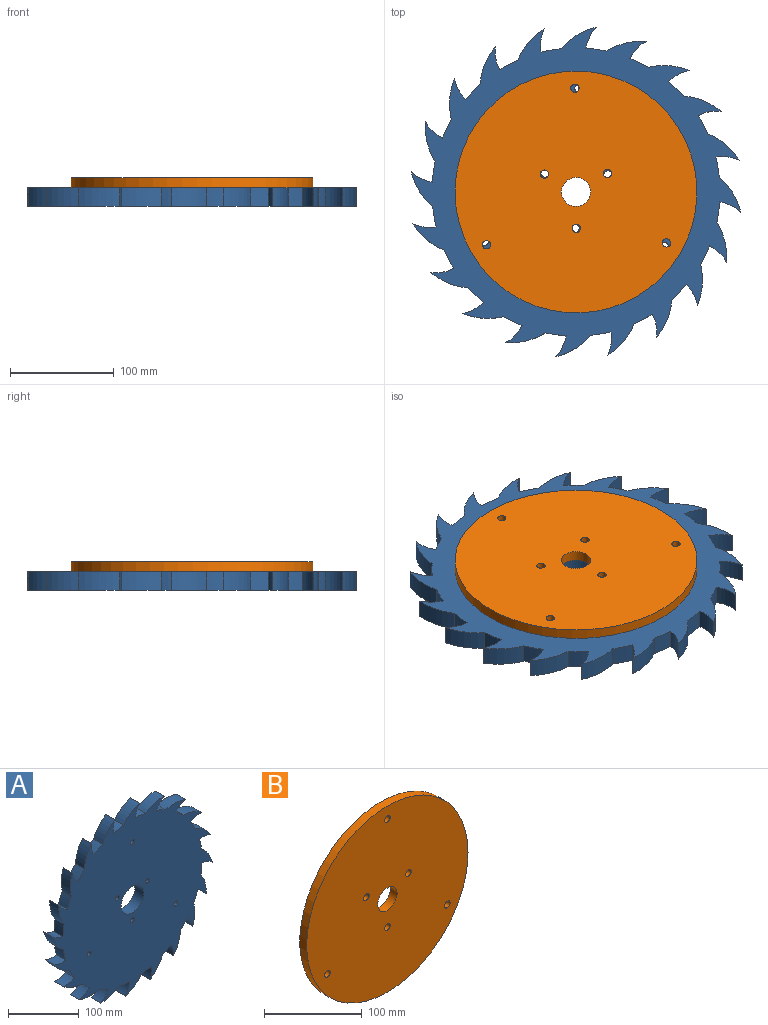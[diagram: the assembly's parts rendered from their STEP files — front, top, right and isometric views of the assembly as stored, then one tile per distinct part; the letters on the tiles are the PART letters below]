
ASSEMBLY  parts=2 mates=1
PART A: 69 faces, bbox 318.6x18x318.6 mm
  f0: cylinder r=138.84mm len=19.46mm, axis (0,1,0), area 357.8mm2, adj f1,f66,f67,f68
  f1: cylinder r=38.2mm len=22.42mm, axis (0,1,0), area 412mm2, adj f0,f2,f67,f68
  f2: cylinder r=63.8mm len=30.75mm, axis (0,1,0), area 720.6mm2, adj f1,f3,f67,f68
  f3: cylinder r=138.84mm len=18mm, axis (0,1,0), area 357.8mm2, adj f2,f4,f67,f68
  f4: cylinder r=38.2mm len=22.06mm, axis (0,1,0), area 412mm2, adj f3,f5,f67,f68
  f5: cylinder r=63.8mm len=36.85mm, axis (0,1,0), area 720.6mm2, adj f4,f6,f67,f68
  f6: cylinder r=138.84mm len=18mm, axis (0,1,0), area 357.8mm2, adj f5,f7,f67,f68
  f7: cylinder r=38.2mm len=19.55mm, axis (0,1,0), area 412mm2, adj f6,f8,f67,f68
  f8: cylinder r=63.8mm len=39.34mm, axis (0,1,0), area 720.6mm2, adj f7,f9,f67,f68
  f9: cylinder r=138.84mm len=18.08mm, axis (0,1,0), area 357.8mm2, adj f8,f10,f67,f68
  f10: cylinder r=38.2mm len=18mm, axis (0,1,0), area 412mm2, adj f9,f11,f67,f68
  f11: cylinder r=63.8mm len=37.98mm, axis (0,1,0), area 720.6mm2, adj f10,f12,f67,f68
  f12: cylinder r=138.84mm len=19.73mm, axis (0,1,0), area 357.8mm2, adj f11,f13,f67,f68
  f13: cylinder r=38.2mm len=20.58mm, axis (0,1,0), area 412mm2, adj f12,f14,f67,f68
  f14: cylinder r=63.8mm len=32.9mm, axis (0,1,0), area 720.6mm2, adj f13,f15,f67,f68
  f15: cylinder r=138.84mm len=19.46mm, axis (0,1,0), area 357.8mm2, adj f14,f16,f67,f68
  f16: cylinder r=38.2mm len=22.42mm, axis (0,1,0), area 412mm2, adj f15,f17,f67,f68
  f17: cylinder r=63.8mm len=30.75mm, axis (0,1,0), area 720.6mm2, adj f16,f18,f67,f68
  f18: cylinder r=138.84mm len=18mm, axis (0,1,0), area 357.8mm2, adj f17,f19,f67,f68
  f19: cylinder r=38.2mm len=22.06mm, axis (0,1,0), area 412mm2, adj f18,f20,f67,f68
  f20: cylinder r=63.8mm len=36.85mm, axis (0,1,0), area 720.6mm2, adj f19,f21,f67,f68
  f21: cylinder r=138.84mm len=18mm, axis (0,1,0), area 357.8mm2, adj f20,f22,f67,f68
  f22: cylinder r=38.2mm len=19.55mm, axis (0,1,0), area 412mm2, adj f21,f23,f67,f68
  f23: cylinder r=63.8mm len=39.34mm, axis (0,1,0), area 720.6mm2, adj f22,f24,f67,f68
  f24: cylinder r=138.84mm len=18.08mm, axis (0,1,0), area 357.8mm2, adj f23,f25,f67,f68
  f25: cylinder r=38.2mm len=18mm, axis (0,1,0), area 412mm2, adj f24,f26,f67,f68
  f26: cylinder r=63.8mm len=37.98mm, axis (0,1,0), area 720.6mm2, adj f25,f27,f67,f68
  f27: cylinder r=138.84mm len=19.73mm, axis (0,1,0), area 357.8mm2, adj f26,f28,f67,f68
  f28: cylinder r=38.2mm len=20.58mm, axis (0,1,0), area 412mm2, adj f27,f29,f67,f68
  f29: cylinder r=63.8mm len=32.9mm, axis (0,1,0), area 720.6mm2, adj f28,f30,f67,f68
  f30: cylinder r=138.84mm len=19.46mm, axis (0,1,0), area 357.8mm2, adj f29,f31,f67,f68
  f31: cylinder r=38.2mm len=22.42mm, axis (0,1,0), area 412mm2, adj f30,f32,f67,f68
  f32: cylinder r=63.8mm len=30.75mm, axis (0,1,0), area 720.6mm2, adj f31,f33,f67,f68
  f33: cylinder r=138.84mm len=18mm, axis (0,1,0), area 357.8mm2, adj f32,f34,f67,f68
  f34: cylinder r=38.2mm len=22.06mm, axis (0,1,0), area 412mm2, adj f33,f35,f67,f68
  f35: cylinder r=63.8mm len=36.85mm, axis (0,1,0), area 720.6mm2, adj f34,f36,f67,f68
  f36: cylinder r=138.84mm len=18mm, axis (0,1,0), area 357.8mm2, adj f35,f37,f67,f68
  f37: cylinder r=38.2mm len=19.55mm, axis (0,1,0), area 412mm2, adj f36,f38,f67,f68
  f38: cylinder r=63.8mm len=39.34mm, axis (0,1,0), area 720.6mm2, adj f37,f39,f67,f68
  f39: cylinder r=138.84mm len=18.08mm, axis (0,1,0), area 357.8mm2, adj f38,f40,f67,f68
  f40: cylinder r=38.2mm len=18mm, axis (0,1,0), area 412mm2, adj f39,f41,f67,f68
  f41: cylinder r=63.8mm len=37.98mm, axis (0,1,0), area 720.6mm2, adj f40,f42,f67,f68
  f42: cylinder r=138.84mm len=19.73mm, axis (0,1,0), area 357.8mm2, adj f41,f43,f67,f68
  f43: cylinder r=38.2mm len=20.58mm, axis (0,1,0), area 412mm2, adj f42,f44,f67,f68
  f44: cylinder r=63.8mm len=32.9mm, axis (0,1,0), area 720.6mm2, adj f43,f45,f67,f68
  f45: cylinder r=138.84mm len=19.46mm, axis (0,1,0), area 357.8mm2, adj f44,f46,f67,f68
  f46: cylinder r=38.2mm len=22.42mm, axis (0,1,0), area 412mm2, adj f45,f47,f67,f68
  f47: cylinder r=63.8mm len=30.75mm, axis (0,1,0), area 720.6mm2, adj f46,f48,f67,f68
  f48: cylinder r=138.84mm len=18mm, axis (0,1,0), area 357.8mm2, adj f47,f49,f67,f68
  f49: cylinder r=38.2mm len=22.06mm, axis (0,1,0), area 412mm2, adj f48,f50,f67,f68
  f50: cylinder r=63.8mm len=36.85mm, axis (0,1,0), area 720.6mm2, adj f49,f51,f67,f68
  f51: cylinder r=138.84mm len=18mm, axis (0,1,0), area 357.8mm2, adj f50,f52,f67,f68
  f52: cylinder r=38.2mm len=19.55mm, axis (0,1,0), area 412mm2, adj f51,f53,f67,f68
  f53: cylinder r=63.8mm len=39.34mm, axis (0,1,0), area 720.6mm2, adj f52,f54,f67,f68
  f54: cylinder r=138.84mm len=18.08mm, axis (0,1,0), area 357.8mm2, adj f53,f55,f67,f68
  f55: cylinder r=38.2mm len=18mm, axis (0,1,0), area 412mm2, adj f54,f56,f67,f68
  f56: cylinder r=63.8mm len=37.98mm, axis (0,1,0), area 720.6mm2, adj f55,f57,f67,f68
  f57: cylinder r=138.84mm len=19.73mm, axis (0,1,0), area 357.8mm2, adj f56,f58,f67,f68
  f58: cylinder r=38.2mm len=20.58mm, axis (0,1,0), area 412mm2, adj f57,f66,f67,f68
  f59: cylinder r=4mm len=18mm, axis (0,1,0), area 452.4mm2, adj f67,f68
  f60: cylinder r=22.61mm len=45.21mm, axis (0,1,0), area 2556.7mm2, adj f67,f68
  f61: cylinder r=4mm len=18mm, axis (0,1,0), area 452.4mm2, adj f67,f68
  f62: cylinder r=4mm len=18mm, axis (0,1,0), area 452.4mm2, adj f67,f68
  f63: cylinder r=4mm len=18mm, axis (0,1,0), area 452.4mm2, adj f67,f68
  f64: cylinder r=4mm len=18mm, axis (0,1,0), area 452.4mm2, adj f67,f68
  f65: cylinder r=4mm len=18mm, axis (0,1,0), area 452.4mm2, adj f67,f68
  f66: cylinder r=63.8mm len=32.9mm, axis (0,1,0), area 720.6mm2, adj f0,f58,f67,f68
  f67: plane 318.62x318.62mm, normal (0,-1,0), area 64400.2mm2, adj f0,f1,f2,f3,f4,f5,f6,f7
  f68: plane 318.62x318.62mm, normal (0,1,0), area 64400.2mm2, adj f0,f1,f2,f3,f4,f5,f6,f7
PART B: 10 faces, bbox 233x10x233 mm
  f0: cylinder r=14mm len=28mm, axis (0,1,0), area 879.6mm2, adj f8,f9
  f1: cylinder r=4mm len=10mm, axis (0,1,0), area 251.3mm2, adj f8,f9
  f2: cylinder r=4mm len=10mm, axis (0,1,0), area 251.3mm2, adj f8,f9
  f3: cylinder r=4mm len=10mm, axis (0,1,0), area 251.3mm2, adj f8,f9
  f4: cylinder r=4mm len=10mm, axis (0,1,0), area 251.3mm2, adj f8,f9
  f5: cylinder r=4mm len=10mm, axis (0,1,0), area 251.3mm2, adj f8,f9
  f6: cylinder r=4mm len=10mm, axis (0,1,0), area 251.3mm2, adj f8,f9
  f7: cylinder r=116.5mm len=233mm, axis (0,1,0), area 7319.9mm2, adj f8,f9
  f8: plane 233x233mm, normal (0,-1,0), area 41721.1mm2, adj f0,f1,f2,f3,f4,f5,f6,f7
  f9: plane 233x233mm, normal (0,1,0), area 41721.1mm2, adj f0,f1,f2,f3,f4,f5,f6,f7
PLACE A rot(axis=(-1,0.01,-0.01),90deg) t=(0,0,-18)mm
PLACE B rot(axis=(0,-0.71,-0.71),179.6deg) t=(0,0,9.8)mm
MATE cylindrical A.f0 <-> B.f0  axis (0,0,1) through (0,0,0)mm
